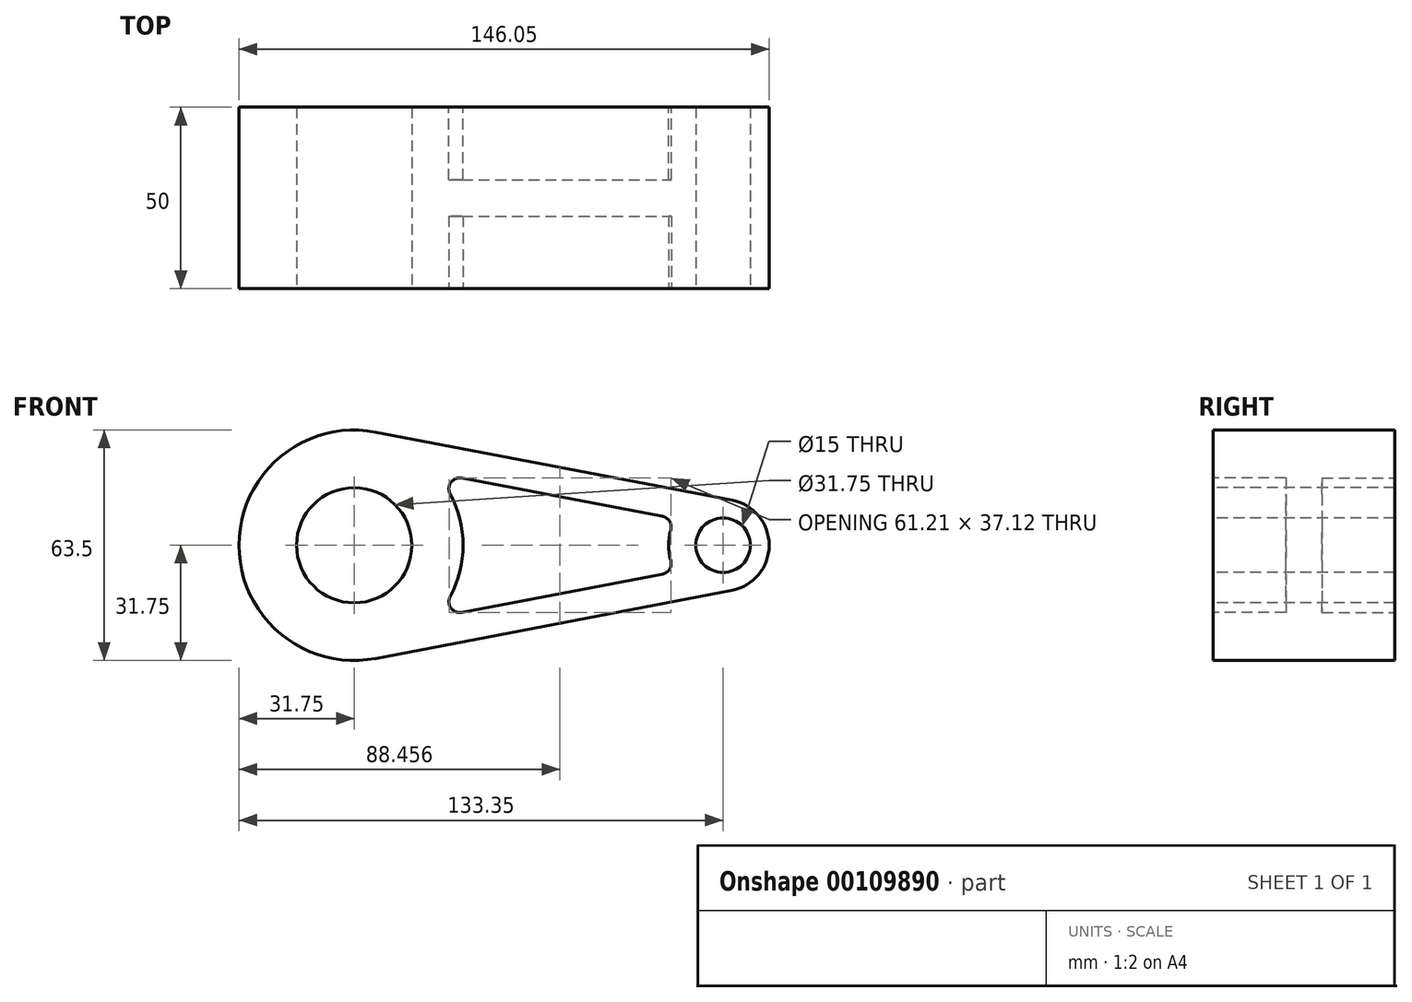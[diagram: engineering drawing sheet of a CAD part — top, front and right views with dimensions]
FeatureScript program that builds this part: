
annotation { "Feature Type Name" : "Feature", "Feature Type Description" : "" }
export const myFeature = defineFeature(function(context is Context, id is Id, definition is map)
    precondition{}
    {
        {
            var Q0;
            Q0=qCreatedBy(makeId("Front.planeOp"),FACE);
            var sketch = newSketch(context, id + "F0", { "sketchPlane" : qUnion([Q0])});
            skArc(sketch, "E0", {"start": v(5.95, 31.19) * mm, "mid": v(-31.75, 0) * mm, "end": v(5.95, -31.19) * mm});
            skArc(sketch, "E1", {"start": v(103.98, -12.47) * mm, "mid": v(114.3, 0) * mm, "end": v(103.98, 12.47) * mm});
            skLineSegment(sketch, "E2", {"start": v(5.95, 31.19) * mm, "end": v(103.98, 12.47) * mm});
            skLineSegment(sketch, "E3", {"start": v(5.95, -31.19) * mm, "end": v(103.98, -12.47) * mm});
            skLineSegment(sketch, "E4", {"start": v(0, 0) * mm, "end": v(101.6, 0) * mm, "construction": true});
            skSolve(sketch);
        }
        {
            var Q0;
            Q0 = qSketchRegion(id + "F0", true);
            extrude(context, id + "F1", {"entities" : qUnion([Q0]), "endBound" : BoundingType.SYMMETRIC, "depth" : 50 * mm});
        }
        {
            var Q0;
            Q0=makeQuery(id+"F1.opExtrude","CAP_FACE",FACE,{"disambiguationData":[OSD([sQuery(id+"F0.wireOp",EDGE,"E0"),sQuery(id+"F0.wireOp",EDGE,"E1"),sQuery(id+"F0.wireOp",EDGE,"E2"),sQuery(id+"F0.wireOp",EDGE,"E3")])],"isStart":false});
            var sketch = newSketch(context, id + "F2", { "sketchPlane" : qUnion([Q0])});
            skPoint(sketch, "E5", {"position": v(101.6, 0) * mm});
            skSolve(sketch);
        }
        {
            var Q0;
            Q0=sQuery(id+"F2.wireOp",VERTEX,"E5");
            var Q1;
            Q1=makeQuery(id+"F1.opExtrude","SWEPT_BODY",BODY,{"disambiguationData":[OSD([sQuery(id+"F0.wireOp",EDGE,"E0"),sQuery(id+"F0.wireOp",EDGE,"E1"),sQuery(id+"F0.wireOp",EDGE,"E2"),sQuery(id+"F0.wireOp",EDGE,"E3")])]});
            hole(context, id + "F3", {"style" : HoleStyle.SIMPLE, "endStyle" : HoleEndStyle.THROUGH, "holeDiameter" : 15 * mm, "locations" : qUnion([Q0]), "scope" : qUnion([Q1]), "isTappedThrough" : true});
        }
        {
            var Q0;
            Q0=makeQuery(id+"F1.opExtrude","CAP_FACE",FACE,{"disambiguationData":[OSD([sQuery(id+"F0.wireOp",EDGE,"E0"),sQuery(id+"F0.wireOp",EDGE,"E1"),sQuery(id+"F0.wireOp",EDGE,"E2"),sQuery(id+"F0.wireOp",EDGE,"E3")])],"isStart":false});
            var sketch = newSketch(context, id + "F4", { "sketchPlane" : qUnion([Q0])});
            skCircle(sketch, "E6", {"center": v(0, 0) * mm, "radius": 15.88 * mm});
            skSolve(sketch);
        }
        {
            var Q0;
            Q0=makeQuery(id+"F4.imprint","IMPRINT",FACE,{"disambiguationData":[TD([[makeQuery(id+"F4.imprint","IMPRINT",EDGE,{"derivedFrom":sQuery(id+"F4.wireOp",EDGE,"E6")}),1.0]])]});
            var Q1;
            Q1=sQuery(id+"F4.wireOp",EDGE,"E6");
            extrude(context, id + "F5", {"entities" : qUnion([Q0]), "operationType" : NewBodyOperationType.REMOVE, "surfaceEntities" : qUnion([Q1]), "endBound" : BoundingType.THROUGH_ALL, "oppositeDirection" : true, "depth" : 25.4 * mm});
        }
        {
            var Q0;
            Q0=makeQuery(id+"F1.opExtrude","CAP_FACE",FACE,{"disambiguationData":[OSD([sQuery(id+"F0.wireOp",EDGE,"E0"),sQuery(id+"F0.wireOp",EDGE,"E1"),sQuery(id+"F0.wireOp",EDGE,"E2"),sQuery(id+"F0.wireOp",EDGE,"E3")])],"isStart":false});
            var sketch = newSketch(context, id + "F6", { "sketchPlane" : qUnion([Q0])});
            skLineSegment(sketch, "E7", {"start": v(22.46, 19.9) * mm, "end": v(88.49, 7.29) * mm});
            skArc(sketch, "E8", {"start": v(88.49, 7.29) * mm, "mid": v(86.6, 0) * mm, "end": v(88.49, -7.29) * mm});
            skLineSegment(sketch, "E9", {"start": v(88.49, -7.29) * mm, "end": v(22.46, -19.9) * mm});
            skArc(sketch, "E10", {"start": v(22.46, -19.9) * mm, "mid": v(30, 0) * mm, "end": v(22.46, 19.9) * mm});
            skSolve(sketch);
        }
        {
            var Q0;
            Q0 = qSketchRegion(id + "F6", true);
            extrude(context, id + "F7", {"entities" : qUnion([Q0]), "operationType" : NewBodyOperationType.REMOVE, "oppositeDirection" : true, "depth" : 20 * mm});
        }
        {
            var Q0;
            Q0=makeQuery(id+"F1.opExtrude","CAP_FACE",FACE,{"disambiguationData":[OSD([sQuery(id+"F0.wireOp",EDGE,"E0"),sQuery(id+"F0.wireOp",EDGE,"E1"),sQuery(id+"F0.wireOp",EDGE,"E2"),sQuery(id+"F0.wireOp",EDGE,"E3")])],"isStart":true});
            var sketch = newSketch(context, id + "F8", { "sketchPlane" : qUnion([Q0])});
            skArc(sketch, "E11.0", {"start": v(-22.46, -19.9) * mm, "mid": v(-30, 0) * mm, "end": v(-22.46, 19.9) * mm});
            skLineSegment(sketch, "E11.1", {"start": v(-22.46, 19.9) * mm, "end": v(-88.49, 7.29) * mm});
            skLineSegment(sketch, "E11.2", {"start": v(-88.49, -7.29) * mm, "end": v(-22.46, -19.9) * mm});
            skArc(sketch, "E11.3", {"start": v(-88.49, 7.29) * mm, "mid": v(-86.6, 0) * mm, "end": v(-88.49, -7.29) * mm});
            skSolve(sketch);
        }
        {
            var Q0;
            Q0 = qSketchRegion(id + "F8", true);
            extrude(context, id + "F9", {"entities" : qUnion([Q0]), "operationType" : NewBodyOperationType.REMOVE, "oppositeDirection" : true, "depth" : 20 * mm});
        }
        {
            var Q0;
            Q0=makeQuery(id+"F7.boolean.opBoolean","COPY",EDGE,{"derivedFrom":makeQuery(id+"F7.opExtrude","SWEPT_EDGE",EDGE,{"disambiguationData":[OSD([sQuery(id+"F6.wireOp",EDGE,"E9"),sQuery(id+"F6.wireOp",EDGE,"E10")])]})});
            var Q1;
            Q1=makeQuery(id+"F7.boolean.opBoolean","COPY",EDGE,{"derivedFrom":makeQuery(id+"F7.opExtrude","SWEPT_EDGE",EDGE,{"disambiguationData":[OSD([sQuery(id+"F6.wireOp",EDGE,"E7"),sQuery(id+"F6.wireOp",EDGE,"E10")])]})});
            var Q2;
            Q2=makeQuery(id+"F9.boolean.opBoolean","COPY",EDGE,{"derivedFrom":makeQuery(id+"F9.opExtrude","SWEPT_EDGE",EDGE,{"disambiguationData":[OSD([sQuery(id+"F8.wireOp",EDGE,"E11.0"),sQuery(id+"F8.wireOp",EDGE,"E11.1")])]})});
            var Q3;
            Q3=makeQuery(id+"F9.boolean.opBoolean","COPY",EDGE,{"derivedFrom":makeQuery(id+"F9.opExtrude","SWEPT_EDGE",EDGE,{"disambiguationData":[OSD([sQuery(id+"F8.wireOp",EDGE,"E11.0"),sQuery(id+"F8.wireOp",EDGE,"E11.2")])]})});
            fillet(context, id + "F10", {"entities" : qUnion([Q0, Q1, Q2, Q3]), "radius" : 3 * mm, "tangentPropagation" : true, "allowEdgeOverflow" : false});
        }
        {
            var Q0;
            Q0=makeQuery(id+"F9.boolean.opBoolean","COPY",EDGE,{"derivedFrom":makeQuery(id+"F9.opExtrude","SWEPT_EDGE",EDGE,{"disambiguationData":[OSD([sQuery(id+"F8.wireOp",EDGE,"E11.2"),sQuery(id+"F8.wireOp",EDGE,"E11.3")])]})});
            var Q1;
            Q1=makeQuery(id+"F9.boolean.opBoolean","COPY",EDGE,{"derivedFrom":makeQuery(id+"F9.opExtrude","SWEPT_EDGE",EDGE,{"disambiguationData":[OSD([sQuery(id+"F8.wireOp",EDGE,"E11.1"),sQuery(id+"F8.wireOp",EDGE,"E11.3")])]})});
            var Q2;
            Q2=makeQuery(id+"F7.boolean.opBoolean","COPY",EDGE,{"derivedFrom":makeQuery(id+"F7.opExtrude","SWEPT_EDGE",EDGE,{"disambiguationData":[OSD([sQuery(id+"F6.wireOp",EDGE,"E7"),sQuery(id+"F6.wireOp",EDGE,"E8")])]})});
            var Q3;
            Q3=makeQuery(id+"F7.boolean.opBoolean","COPY",EDGE,{"derivedFrom":makeQuery(id+"F7.opExtrude","SWEPT_EDGE",EDGE,{"disambiguationData":[OSD([sQuery(id+"F6.wireOp",EDGE,"E8"),sQuery(id+"F6.wireOp",EDGE,"E9")])]})});
            fillet(context, id + "F11", {"entities" : qUnion([Q0, Q1, Q2, Q3]), "radius" : 3 * mm, "tangentPropagation" : true, "allowEdgeOverflow" : false});
        }
    });
